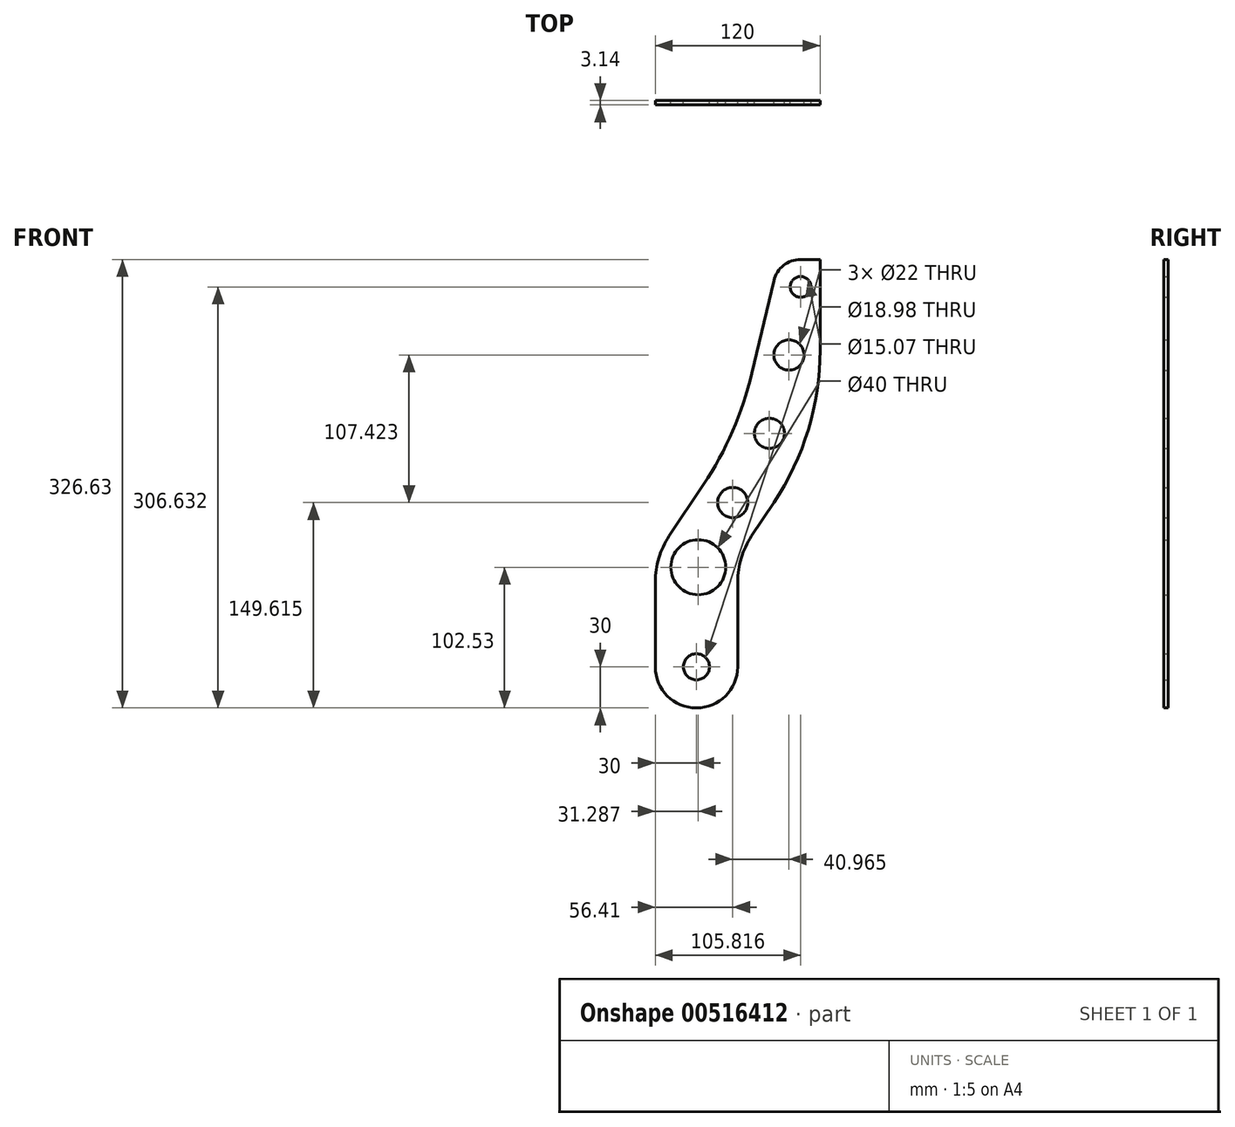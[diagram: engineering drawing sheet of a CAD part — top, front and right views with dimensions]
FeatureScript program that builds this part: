
annotation { "Feature Type Name" : "Feature", "Feature Type Description" : "" }
export const myFeature = defineFeature(function(context is Context, id is Id, definition is map)
    precondition{}
    {
        {
            var Q0;
            Q0=qCreatedBy(makeId("Front.planeOp"),FACE);
            var sketch = newSketch(context, id + "F0", { "sketchPlane" : qUnion([Q0])});
            skLineSegment(sketch, "E0", {"start": v(60, 30) * mm, "end": v(60, 91.83) * mm});
            skLineSegment(sketch, "E1", {"start": v(70.08, 125.12) * mm, "end": v(86.41, 149.62) * mm});
            skLineSegment(sketch, "E2", {"start": v(10.08, 125.12) * mm, "end": v(35.1, 162.64) * mm});
            skLineSegment(sketch, "E3", {"start": v(120, 260.56) * mm, "end": v(120, 326.63) * mm});
            skLineSegment(sketch, "E4", {"start": v(120, 326.63) * mm, "end": v(105.82, 326.63) * mm});
            skLineSegment(sketch, "E5", {"start": v(86.35, 311.24) * mm, "end": v(70.35, 243.69) * mm});
            skLineSegment(sketch, "E6", {"start": v(120, 110) * mm, "end": v(120, 110) * mm});
            skPoint(sketch, "E7.orphan", {"position": v(0, 200) * mm});
            skPoint(sketch, "E8.end.orphan", {"position": v(60, 110) * mm});
            skPoint(sketch, "E9.visualSharp", {"position": v(60, 200) * mm});
            skArc(sketch, "E9.filletArc", {"start": v(35.1, 162.64) * mm, "mid": v(56.33, 201.6) * mm, "end": v(70.35, 243.69) * mm});
            skPoint(sketch, "E10.visualSharp", {"position": v(120, 200) * mm});
            skArc(sketch, "E10.filletArc", {"start": v(86.41, 149.62) * mm, "mid": v(111.42, 202.6) * mm, "end": v(120, 260.56) * mm});
            skArc(sketch, "E11.filletArc", {"start": v(70.08, 125.12) * mm, "mid": v(62.57, 109.22) * mm, "end": v(60, 91.83) * mm});
            skLineSegment(sketch, "E12", {"start": v(30, 0) * mm, "end": v(30, 0) * mm});
            skLineSegment(sketch, "E13", {"start": v(0, 30) * mm, "end": v(0, 91.83) * mm});
            skPoint(sketch, "E14.visualSharp", {"position": v(0, 110) * mm});
            skArc(sketch, "E14.filletArc", {"start": v(10.08, 125.12) * mm, "mid": v(2.57, 109.22) * mm, "end": v(0, 91.83) * mm});
            skPoint(sketch, "E15.visualSharp", {"position": v(90, 326.63) * mm});
            skArc(sketch, "E15.filletArc", {"start": v(105.82, 326.63) * mm, "mid": v(93.41, 322.32) * mm, "end": v(86.35, 311.24) * mm});
            skPoint(sketch, "E16.visualSharp", {"position": v(60, 0) * mm});
            skArc(sketch, "E16.filletArc", {"start": v(30, 0) * mm, "mid": v(51.21, 8.79) * mm, "end": v(60, 30) * mm});
            skPoint(sketch, "E17.visualSharp", {"position": v(0, 0) * mm});
            skArc(sketch, "E17.filletArc", {"start": v(0, 30) * mm, "mid": v(8.79, 8.79) * mm, "end": v(30, 0) * mm});
            skCircle(sketch, "E18", {"center": v(30, 30) * mm, "radius": 9.49 * mm});
            skCircle(sketch, "E19", {"center": v(56.41, 149.62) * mm, "radius": 11 * mm});
            skPoint(sketch, "E20.orphan", {"position": v(26.41, 149.62) * mm});
            skCircle(sketch, "E21", {"center": v(83.12, 200) * mm, "radius": 11 * mm});
            skPoint(sketch, "E22.trimOffspring.end.orphan", {"position": v(55.63, 200) * mm});
            skPoint(sketch, "E23.start.orphan", {"position": v(110.61, 200) * mm});
            skCircle(sketch, "E24", {"center": v(105.82, 306.63) * mm, "radius": 7.53 * mm});
            skPoint(sketch, "E25.center.orphan", {"position": v(30, 110) * mm});
            skPoint(sketch, "E26.centerSnap0", {"position": v(31.29, 109.61) * mm});
            skPoint(sketch, "E27.orphan", {"position": v(62.57, 109.22) * mm});
            skLineSegment(sketch, "E28.trimOffspring", {"start": v(2.8, 109.97) * mm, "end": v(0, 110) * mm});
            skCircle(sketch, "E29", {"center": v(97.38, 257.04) * mm, "radius": 11 * mm});
            skPoint(sketch, "E26.center.orphan", {"position": v(31.29, 110) * mm});
            skCircle(sketch, "E30", {"center": v(31.29, 102.53) * mm, "radius": 20 * mm});
            skSolve(sketch);
        }
        {
            var Q0;
            Q0=makeQuery(id+"F0.imprint","IMPRINT",FACE,{"disambiguationData":[TD([[makeQuery(id+"F0.imprint","IMPRINT",EDGE,{"derivedFrom":sQuery(id+"F0.wireOp",EDGE,"E0")}),1.0]])]});
            extrude(context, id + "F1", {"entities" : qUnion([Q0]), "depth" : 3.14 * mm, "offsetDistance" : 25 * mm});
        }
    });
